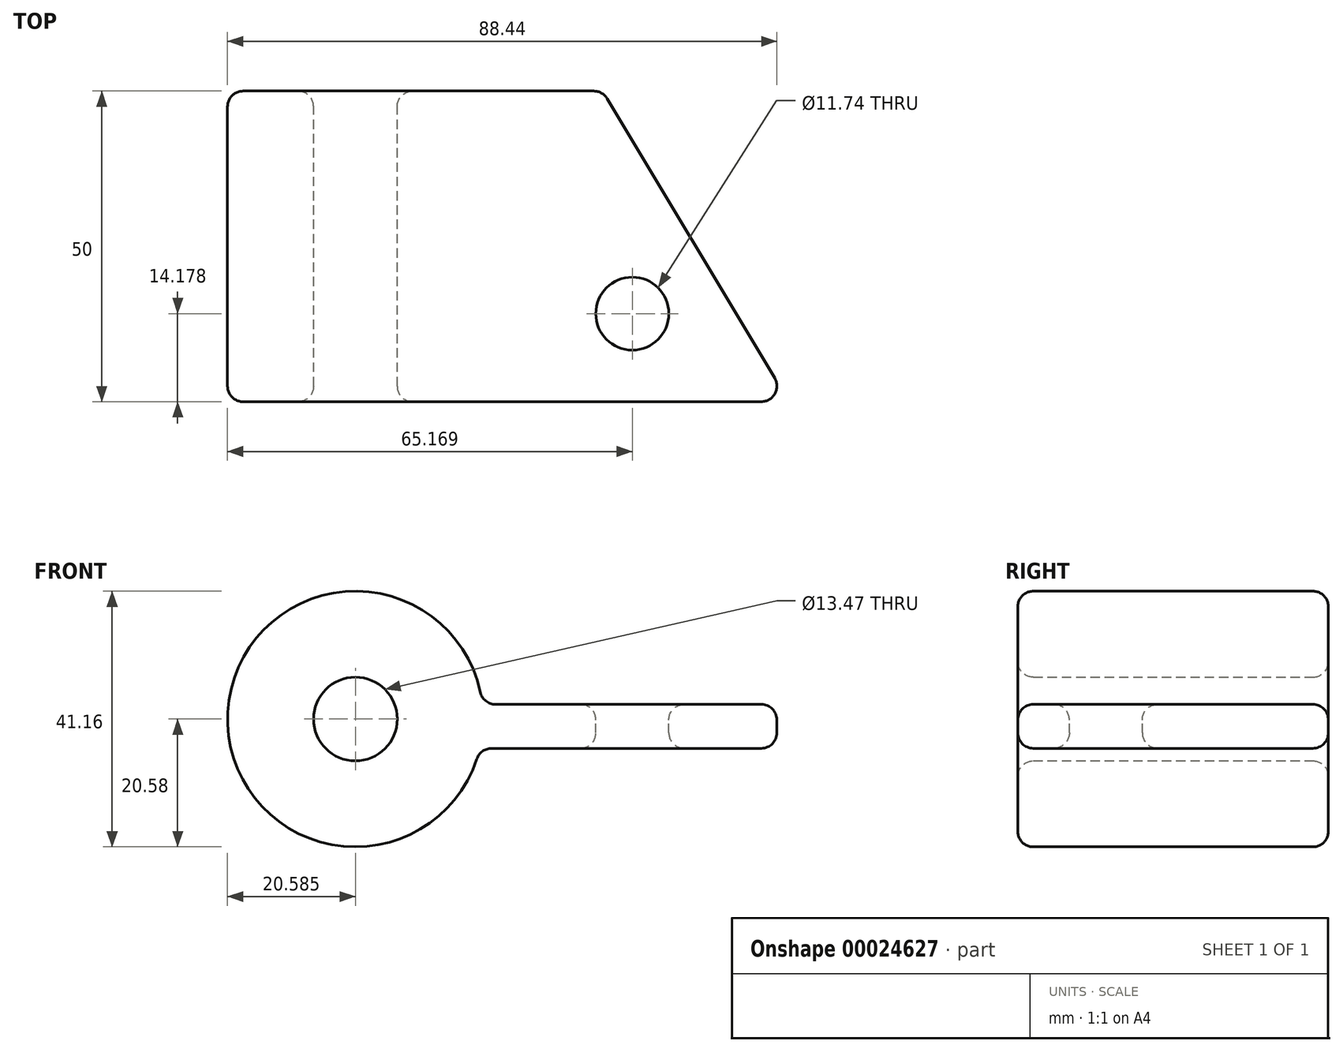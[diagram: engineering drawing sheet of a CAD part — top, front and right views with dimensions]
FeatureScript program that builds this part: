
annotation { "Feature Type Name" : "Feature", "Feature Type Description" : "" }
export const myFeature = defineFeature(function(context is Context, id is Id, definition is map)
    precondition{}
    {
        {
            var Q0;
            Q0=qCreatedBy(makeId("Front.planeOp"),FACE);
            var sketch = newSketch(context, id + "F0", { "sketchPlane" : qUnion([Q0])});
            skCircle(sketch, "E0", {"center": v(-44.76, 6.82) * mm, "radius": 20.58 * mm});
            skCircle(sketch, "E1", {"center": v(-44.76, 6.82) * mm, "radius": 6.74 * mm});
            skSolve(sketch);
        }
        {
            var Q0;
            Q0=makeQuery(id+"F0.imprint","IMPRINT",FACE,{"disambiguationData":[TD([[makeQuery(id+"F0.imprint","IMPRINT",EDGE,{"derivedFrom":sQuery(id+"F0.wireOp",EDGE,"E0")}),1.0]])]});
            extrude(context, id + "F1", {"entities" : qUnion([Q0]), "depth" : 50 * mm});
        }
        {
            var Q0;
            Q0=qCreatedBy(makeId("Right.planeOp"),FACE);
            var sketch = newSketch(context, id + "F2", { "sketchPlane" : qUnion([Q0])});
            skLineSegment(sketch, "E2.bottom", {"start": v(-50.14, 9.18) * mm, "end": v(0, 9.18) * mm});
            skLineSegment(sketch, "E2.top", {"start": v(-50.14, 2.1) * mm, "end": v(0, 2.1) * mm});
            skLineSegment(sketch, "E2.left", {"start": v(-50.14, 9.18) * mm, "end": v(-50.14, 2.1) * mm});
            skLineSegment(sketch, "E2.right", {"start": v(0, 9.18) * mm, "end": v(0, 2.1) * mm});
            skSolve(sketch);
        }
        {
            var Q0;
            Q0=makeQuery(id+"F2.imprint","IMPRINT",FACE,{"disambiguationData":[TD([[makeQuery(id+"F2.imprint","IMPRINT",EDGE,{"derivedFrom":sQuery(id+"F2.wireOp",EDGE,"E2.bottom")}),-1.0]])]});
            extrude(context, id + "F3", {"entities" : qUnion([Q0]), "oppositeDirection" : true, "depth" : 25 * mm});
        }
        {
            var Q0;
            Q0=makeQuery(id+"F3.opExtrude","SWEPT_BODY",BODY,{"disambiguationData":[OSD([sQuery(id+"F2.wireOp",EDGE,"E2.bottom"),sQuery(id+"F2.wireOp",EDGE,"E2.top"),sQuery(id+"F2.wireOp",EDGE,"E2.left"),sQuery(id+"F2.wireOp",EDGE,"E2.right")])]});
            var Q1;
            Q1=makeQuery(id+"F1.opExtrude","SWEPT_BODY",BODY,{"disambiguationData":[OSD([sQuery(id+"F0.wireOp",EDGE,"E0"),sQuery(id+"F0.wireOp",EDGE,"E1")])]});
            booleanBodies(context, id + "F4", {"operationType" : BooleanOperationType.UNION, "tools" : qUnion([Q0, Q1])});
        }
        {
            var Q0;
            Q0=makeQuery(id+"F3.opExtrude","CAP_FACE",FACE,{"disambiguationData":[OSD([sQuery(id+"F2.wireOp",EDGE,"E2.bottom"),sQuery(id+"F2.wireOp",EDGE,"E2.top"),sQuery(id+"F2.wireOp",EDGE,"E2.left"),sQuery(id+"F2.wireOp",EDGE,"E2.right")])],"isStart":true});
            extrude(context, id + "F5", {"entities" : qUnion([Q0]), "operationType" : NewBodyOperationType.ADD, "depth" : 25 * mm});
        }
        {
            var Q0;
            {var subQ0=sQuery(id+"F2.wireOp",EDGE,"E2.left");Q0=makeQuery(id+"F5.boolean.opBoolean","MERGE",FACE,{"derivedFrom":[makeQuery(id+"F3.opExtrude","SWEPT_FACE",FACE,{"disambiguationData":[OSD([subQ0])]}),makeQuery(id+"F5.opExtrude","SWEPT_FACE",FACE,{"disambiguationData":[OSD([subQ0])]})]});}
            var Q1;
            Q1=makeQuery(id+"F1.opExtrude","CAP_FACE",FACE,{"disambiguationData":[OSD([sQuery(id+"F0.wireOp",EDGE,"E0"),sQuery(id+"F0.wireOp",EDGE,"E1")])],"isStart":false});
            extrude(context, id + "F6", {"entities" : qUnion([Q0]), "operationType" : NewBodyOperationType.REMOVE, "endBound" : BoundingType.UP_TO_SURFACE, "oppositeDirection" : true, "endBoundEntityFace" : qUnion([Q1]), "depth" : 25 * mm});
        }
        {
            var Q0;
            {var subQ0=sQuery(id+"F2.wireOp",EDGE,"E2.bottom");Q0=makeQuery(id+"F5.boolean.opBoolean","MERGE",FACE,{"derivedFrom":[makeQuery(id+"F3.opExtrude","SWEPT_FACE",FACE,{"disambiguationData":[OSD([subQ0])]}),makeQuery(id+"F5.opExtrude","SWEPT_FACE",FACE,{"disambiguationData":[OSD([subQ0])]})]});}
            var sketch = newSketch(context, id + "F7", { "sketchPlane" : qUnion([Q0])});
            skLineSegment(sketch, "E3", {"start": v(25, -50) * mm, "end": v(-4.96, 0) * mm});
            skSolve(sketch);
        }
        {
            var Q0;
            {var subQ3=sQuery(id+"F7.wireOp",EDGE,"E3");Q0=makeQuery(id+"F7.imprint","IMPRINT",FACE,{"disambiguationData":[TD([[makeQuery(id+"F7.imprint","IMPRINT",EDGE,{"derivedFrom":subQ3}),-1.0]])]});}
            extrude(context, id + "F8", {"entities" : qUnion([Q0]), "operationType" : NewBodyOperationType.REMOVE, "endBound" : BoundingType.THROUGH_ALL, "oppositeDirection" : true, "depth" : 25 * mm});
        }
        {
            var Q0;
            {var subQ0=sQuery(id+"F2.wireOp",EDGE,"E2.bottom");Q0=makeQuery(id+"F5.boolean.opBoolean","MERGE",FACE,{"derivedFrom":[makeQuery(id+"F3.opExtrude","SWEPT_FACE",FACE,{"disambiguationData":[OSD([subQ0])]}),makeQuery(id+"F5.opExtrude","SWEPT_FACE",FACE,{"disambiguationData":[OSD([subQ0])]})]});}
            var sketch = newSketch(context, id + "F9", { "sketchPlane" : qUnion([Q0])});
            skCircle(sketch, "E4", {"center": v(-0.18, -35.82) * mm, "radius": 5.87 * mm});
            skSolve(sketch);
        }
        {
            var Q0;
            Q0=makeQuery(id+"F9.imprint","IMPRINT",FACE,{"disambiguationData":[TD([[makeQuery(id+"F9.imprint","IMPRINT",EDGE,{"derivedFrom":sQuery(id+"F9.wireOp",EDGE,"E4")}),1.0]])]});
            extrude(context, id + "F10", {"entities" : qUnion([Q0]), "operationType" : NewBodyOperationType.REMOVE, "endBound" : BoundingType.THROUGH_ALL, "oppositeDirection" : true, "depth" : 25 * mm});
        }
        {
            var Q0;
            Q0=makeQuery(id+"F10.boolean.opBoolean","COPY",FACE,{"derivedFrom":makeQuery(id+"F10.opExtrude","SWEPT_FACE",FACE,{"disambiguationData":[OSD([sQuery(id+"F9.wireOp",EDGE,"E4")])]})});
            var Q1;
            Q1=makeQuery(id+"F8.boolean.opBoolean","COPY",FACE,{"derivedFrom":makeQuery(id+"F8.opExtrude","SWEPT_FACE",FACE,{"disambiguationData":[OSD([sQuery(id+"F7.wireOp",EDGE,"E3")])]})});
            var Q2;
            {var subQ0=sQuery(id+"F2.wireOp",EDGE,"E2.bottom");Q2=makeQuery(id+"F5.boolean.opBoolean","MERGE",FACE,{"derivedFrom":[makeQuery(id+"F3.opExtrude","SWEPT_FACE",FACE,{"disambiguationData":[OSD([subQ0])]}),makeQuery(id+"F5.opExtrude","SWEPT_FACE",FACE,{"disambiguationData":[OSD([subQ0])]})]});}
            var Q3;
            Q3=makeQuery(id+"F10.boolean.opBoolean","COPY",EDGE,{"derivedFrom":makeQuery(id+"F10.opExtrude","CAP_EDGE",EDGE,{"disambiguationData":[OSD([sQuery(id+"F9.wireOp",EDGE,"E4")])],"isStart":true})});
            var Q4;
            {var subQ0=sQuery(id+"F2.wireOp",EDGE,"E2.top");Q4=makeQuery(id+"F5.boolean.opBoolean","MERGE",FACE,{"derivedFrom":[makeQuery(id+"F3.opExtrude","SWEPT_FACE",FACE,{"disambiguationData":[OSD([subQ0])]}),makeQuery(id+"F5.opExtrude","SWEPT_FACE",FACE,{"disambiguationData":[OSD([subQ0])]})]});}
            var Q5;
            {var subQ0=sQuery(id+"F2.wireOp",EDGE,"E2.right");Q5=makeQuery(id+"F5.boolean.opBoolean","MERGE",FACE,{"derivedFrom":[makeQuery(id+"F4.opBoolean","MERGE",FACE,{"derivedFrom":[makeQuery(id+"F1.opExtrude","CAP_FACE",FACE,{"disambiguationData":[OSD([sQuery(id+"F0.wireOp",EDGE,"E0"),sQuery(id+"F0.wireOp",EDGE,"E1")])],"isStart":true}),makeQuery(id+"F3.opExtrude","SWEPT_FACE",FACE,{"disambiguationData":[OSD([subQ0])]})]}),makeQuery(id+"F5.opExtrude","SWEPT_FACE",FACE,{"disambiguationData":[OSD([subQ0])]})]});}
            var Q6;
            Q6=makeQuery(id+"F6.boolean.opBoolean","MERGE",FACE,{"derivedFrom":[makeQuery(id+"F1.opExtrude","CAP_FACE",FACE,{"disambiguationData":[OSD([sQuery(id+"F0.wireOp",EDGE,"E0"),sQuery(id+"F0.wireOp",EDGE,"E1")])],"isStart":false}),makeQuery(id+"F6.opExtrude","CAP_FACE",FACE,{"disambiguationData":[OSD([sQuery(id+"F2.wireOp",EDGE,"E2.left")])],"isStart":false})]});
            var Q7;
            {var subQ0=sQuery(id+"F2.wireOp",EDGE,"E2.left");Q7=makeQuery(id+"F8.boolean.opBoolean","MERGE",EDGE,{"derivedFrom":[makeQuery(id+"F6.boolean.opBoolean","COPY",EDGE,{"derivedFrom":makeQuery(id+"F6.opExtrude","CAP_EDGE",EDGE,{"disambiguationData":[OSD([subQ0]),TDD([makeQuery(id+"F5.opExtrude","CAP_EDGE",EDGE,{"disambiguationData":[OSD([subQ0])],"isStart":false})])],"isStart":false})}),makeQuery(id+"F8.opExtrude","SWEPT_EDGE",EDGE,{"disambiguationData":[OSD([sQuery(id+"F2.wireOp",EDGE,"E2.bottom"),subQ0,sQuery(id+"F7.wireOp",EDGE,"E3")])]})]});}
            var Q8;
            Q8=makeQuery(id+"F1.opExtrude","CAP_EDGE",EDGE,{"disambiguationData":[OSD([sQuery(id+"F0.wireOp",EDGE,"E0")])],"isStart":true});
            var Q9;
            Q9=makeQuery(id+"F6.boolean.opBoolean","COPY",EDGE,{"derivedFrom":makeQuery(id+"F6.opExtrude","CAP_EDGE",EDGE,{"disambiguationData":[OSD([sQuery(id+"F2.wireOp",EDGE,"E2.bottom"),sQuery(id+"F2.wireOp",EDGE,"E2.left")])],"isStart":false})});
            var Q10;
            Q10=makeQuery(id+"F1.opExtrude","SWEPT_FACE",FACE,{"disambiguationData":[OSD([sQuery(id+"F0.wireOp",EDGE,"E0")])]});
            var Q11;
            Q11=makeQuery(id+"F6.boolean.opBoolean","COPY",EDGE,{"derivedFrom":makeQuery(id+"F6.opExtrude","CAP_EDGE",EDGE,{"disambiguationData":[OSD([sQuery(id+"F2.wireOp",EDGE,"E2.top"),sQuery(id+"F2.wireOp",EDGE,"E2.left")])],"isStart":false})});
            var Q12;
            Q12=makeQuery(id+"F1.opExtrude","CAP_EDGE",EDGE,{"disambiguationData":[OSD([sQuery(id+"F0.wireOp",EDGE,"E0")])],"isStart":false});
            var Q13;
            Q13=makeQuery(id+"F8.boolean.opBoolean","COPY",EDGE,{"derivedFrom":makeQuery(id+"F8.opExtrude","CAP_EDGE",EDGE,{"disambiguationData":[OSD([sQuery(id+"F7.wireOp",EDGE,"E3")])],"isStart":true})});
            var Q14;
            {var subQ0=sQuery(id+"F2.wireOp",EDGE,"E2.bottom");var subQ1=sQuery(id+"F2.wireOp",EDGE,"E2.right");Q14=makeQuery(id+"F5.boolean.opBoolean","MERGE",EDGE,{"derivedFrom":[makeQuery(id+"F3.opExtrude","SWEPT_EDGE",EDGE,{"disambiguationData":[OSD([subQ0,subQ1])]}),makeQuery(id+"F5.opExtrude","SWEPT_EDGE",EDGE,{"disambiguationData":[OSD([subQ0,subQ1])]})]});}
            var Q15;
            Q15=makeQuery(id+"F1.opExtrude","SWEPT_FACE",FACE,{"disambiguationData":[OSD([sQuery(id+"F0.wireOp",EDGE,"E1")])]});
            var Q16;
            Q16=makeQuery(id+"F1.opExtrude","CAP_EDGE",EDGE,{"disambiguationData":[OSD([sQuery(id+"F0.wireOp",EDGE,"E1")])],"isStart":false});
            var Q17;
            Q17=makeQuery(id+"F4.opBoolean","INTERSECT",EDGE,{"derivedFrom":[makeQuery(id+"F1.opExtrude","SWEPT_FACE",FACE,{"disambiguationData":[OSD([sQuery(id+"F0.wireOp",EDGE,"E0")])]}),makeQuery(id+"F3.opExtrude","SWEPT_FACE",FACE,{"disambiguationData":[OSD([sQuery(id+"F2.wireOp",EDGE,"E2.bottom")])]})]});
            var Q18;
            {var subQ0=sQuery(id+"F2.wireOp",EDGE,"E2.top");Q18=makeQuery(id+"F10.boolean.opBoolean","INTERSECT",EDGE,{"derivedFrom":[makeQuery(id+"F5.boolean.opBoolean","MERGE",FACE,{"derivedFrom":[makeQuery(id+"F3.opExtrude","SWEPT_FACE",FACE,{"disambiguationData":[OSD([subQ0])]}),makeQuery(id+"F5.opExtrude","SWEPT_FACE",FACE,{"disambiguationData":[OSD([subQ0])]})]}),makeQuery(id+"F10.opExtrude","SWEPT_FACE",FACE,{"disambiguationData":[OSD([sQuery(id+"F9.wireOp",EDGE,"E4")])]})]});}
            var Q19;
            {var subQ0=sQuery(id+"F2.wireOp",EDGE,"E2.top");Q19=makeQuery(id+"F8.boolean.opBoolean","INTERSECT",EDGE,{"derivedFrom":[makeQuery(id+"F5.boolean.opBoolean","MERGE",FACE,{"derivedFrom":[makeQuery(id+"F3.opExtrude","SWEPT_FACE",FACE,{"disambiguationData":[OSD([subQ0])]}),makeQuery(id+"F5.opExtrude","SWEPT_FACE",FACE,{"disambiguationData":[OSD([subQ0])]})]}),makeQuery(id+"F8.opExtrude","SWEPT_FACE",FACE,{"disambiguationData":[OSD([sQuery(id+"F7.wireOp",EDGE,"E3")])]})]});}
            var Q20;
            Q20=makeQuery(id+"F8.boolean.opBoolean","COPY",EDGE,{"derivedFrom":makeQuery(id+"F8.opExtrude","SWEPT_EDGE",EDGE,{"disambiguationData":[OSD([sQuery(id+"F2.wireOp",EDGE,"E2.bottom"),sQuery(id+"F2.wireOp",EDGE,"E2.right"),sQuery(id+"F7.wireOp",EDGE,"E3")])]})});
            var Q21;
            {var subQ0=sQuery(id+"F2.wireOp",EDGE,"E2.top");var subQ1=sQuery(id+"F2.wireOp",EDGE,"E2.right");Q21=makeQuery(id+"F5.boolean.opBoolean","MERGE",EDGE,{"derivedFrom":[makeQuery(id+"F3.opExtrude","SWEPT_EDGE",EDGE,{"disambiguationData":[OSD([subQ0,subQ1])]}),makeQuery(id+"F5.opExtrude","SWEPT_EDGE",EDGE,{"disambiguationData":[OSD([subQ0,subQ1])]})]});}
            var Q22;
            Q22=makeQuery(id+"F1.opExtrude","CAP_EDGE",EDGE,{"disambiguationData":[OSD([sQuery(id+"F0.wireOp",EDGE,"E1")])],"isStart":true});
            var Q23;
            Q23=makeQuery(id+"F4.opBoolean","INTERSECT",EDGE,{"derivedFrom":[makeQuery(id+"F1.opExtrude","SWEPT_FACE",FACE,{"disambiguationData":[OSD([sQuery(id+"F0.wireOp",EDGE,"E0")])]}),makeQuery(id+"F3.opExtrude","SWEPT_FACE",FACE,{"disambiguationData":[OSD([sQuery(id+"F2.wireOp",EDGE,"E2.top")])]})]});
            fillet(context, id + "F11", {"entities" : qUnion([Q0, Q1, Q2, Q3, Q4, Q5, Q6, Q7, Q8, Q9, Q10, Q11, Q12, Q13, Q14, Q15, Q16, Q17, Q18, Q19, Q20, Q21, Q22, Q23]), "radius" : 2.5 * mm, "tangentPropagation" : true, "allowEdgeOverflow" : false});
        }
    });
